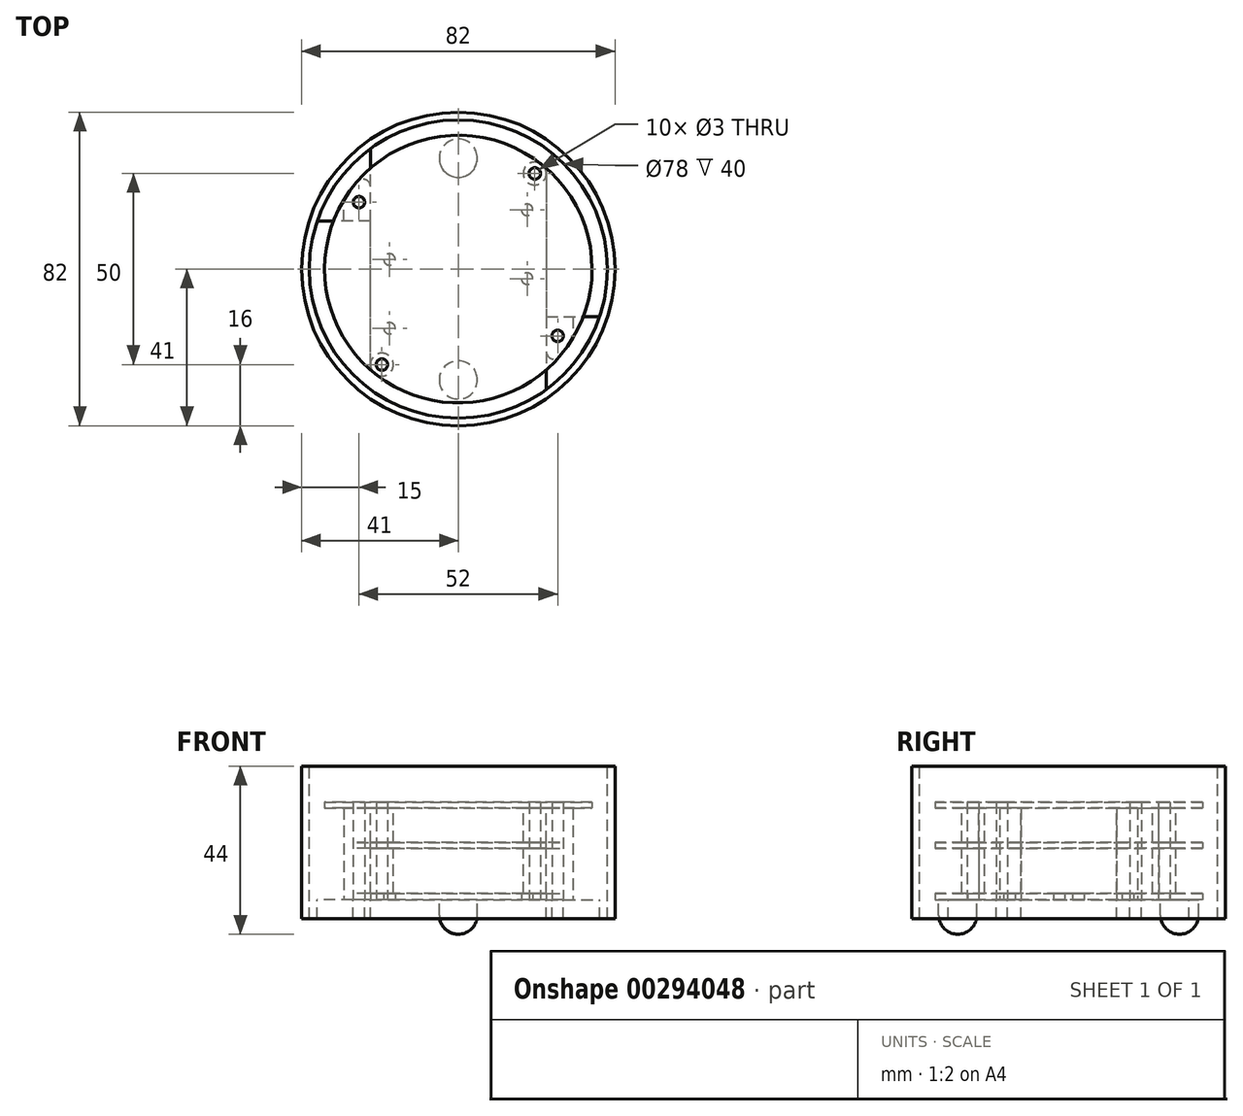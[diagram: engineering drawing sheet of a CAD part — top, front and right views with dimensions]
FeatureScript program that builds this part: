
annotation { "Feature Type Name" : "Feature", "Feature Type Description" : "" }
export const myFeature = defineFeature(function(context is Context, id is Id, definition is map)
    precondition{}
    {
        {
            var Q0;
            Q0=qCreatedBy(makeId("Top.planeOp"),FACE);
            var sketch = newSketch(context, id + "F0", { "sketchPlane" : qUnion([Q0])});
            skPoint(sketch, "E0.middle", {"position": v(0, 0) * mm});
            skLineSegment(sketch, "E1", {"start": v(0, 0) * mm, "end": v(0, 30) * mm, "construction": true});
            skLineSegment(sketch, "E2", {"start": v(0, 0) * mm, "end": v(-11.22, 0) * mm, "construction": true});
            skCircle(sketch, "E3", {"center": v(-18, 2.5) * mm, "radius": 1.5 * mm});
            skCircle(sketch, "E4", {"center": v(-18, -15.5) * mm, "radius": 1.5 * mm});
            skLineSegment(sketch, "E5", {"start": v(-18, -15.5) * mm, "end": v(-18, 2.5) * mm, "construction": true});
            skCircle(sketch, "E6.1.0", {"center": v(18, -2.5) * mm, "radius": 1.5 * mm});
            skCircle(sketch, "E6.1.1", {"center": v(18, 15.5) * mm, "radius": 1.5 * mm});
            skLineSegment(sketch, "E7", {"start": v(-23, -26.38) * mm, "end": v(-23, 12.5) * mm});
            skLineSegment(sketch, "E8", {"start": v(-23, 12.5) * mm, "end": v(-30, 12.5) * mm});
            skLineSegment(sketch, "E9", {"start": v(-30, 12.5) * mm, "end": v(-30, 18.03) * mm});
            skArc(sketch, "E10", {"start": v(-23, -26.38) * mm, "mid": v(5.45, -34.57) * mm, "end": v(30, -18.03) * mm});
            skLineSegment(sketch, "E11.1.0", {"start": v(23, 26.38) * mm, "end": v(23, -12.5) * mm});
            skLineSegment(sketch, "E11.1.1", {"start": v(23, -12.5) * mm, "end": v(30, -12.5) * mm});
            skLineSegment(sketch, "E11.1.2", {"start": v(30, -12.5) * mm, "end": v(30, -18.03) * mm});
            skArc(sketch, "E12.trimOffspring", {"start": v(23, 26.38) * mm, "mid": v(-5.45, 34.57) * mm, "end": v(-30, 18.03) * mm});
            skLineSegment(sketch, "E13", {"start": v(-18, -6.5) * mm, "end": v(-34.57, -6.5) * mm, "construction": true});
            skPoint(sketch, "E13.endSnap0", {"position": v(-18, -6.5) * mm});
            skCircle(sketch, "E14", {"center": v(26, -17.5) * mm, "radius": 1.5 * mm});
            skCircle(sketch, "E15.1.0", {"center": v(-26, 17.5) * mm, "radius": 1.5 * mm});
            skCircle(sketch, "E16", {"center": v(20, 25) * mm, "radius": 1.5 * mm});
            skCircle(sketch, "E17.1.0", {"center": v(-20, -25) * mm, "radius": 1.5 * mm});
            skSolve(sketch);
        }
        {
            var Q0;
            Q0=makeQuery(id+"F0.imprint","IMPRINT",FACE,{"disambiguationData":[TD([[makeQuery(id+"F0.imprint","IMPRINT",EDGE,{"derivedFrom":sQuery(id+"F0.wireOp",EDGE,"E3")}),-1.0]])]});
            extrude(context, id + "F1", {"entities" : qUnion([Q0]), "depth" : 1.67 * mm});
        }
        {
            var Q0;
            Q0=makeQuery(id+"F1.opExtrude","CAP_FACE",FACE,{"disambiguationData":[OSD([sQuery(id+"F0.wireOp",EDGE,"E3"),sQuery(id+"F0.wireOp",EDGE,"E4"),sQuery(id+"F0.wireOp",EDGE,"E6.1.0"),sQuery(id+"F0.wireOp",EDGE,"E6.1.1"),sQuery(id+"F0.wireOp",EDGE,"E7"),sQuery(id+"F0.wireOp",EDGE,"E8"),sQuery(id+"F0.wireOp",EDGE,"E9"),sQuery(id+"F0.wireOp",EDGE,"E10"),sQuery(id+"F0.wireOp",EDGE,"E11.1.0"),sQuery(id+"F0.wireOp",EDGE,"E11.1.1"),sQuery(id+"F0.wireOp",EDGE,"E11.1.2"),sQuery(id+"F0.wireOp",EDGE,"E12.trimOffspring")])],"isStart":true});
            var sketch = newSketch(context, id + "F2", { "sketchPlane" : qUnion([Q0])});
            skLineSegment(sketch, "E18", {"start": v(0, 0) * mm, "end": v(-11.39, 0) * mm, "construction": true});
            skCircle(sketch, "E19", {"center": v(0, 29) * mm, "radius": 5 * mm});
            skLineSegment(sketch, "E20", {"start": v(0, 29) * mm, "end": v(0, 0) * mm, "construction": true});
            skCircle(sketch, "E21.MirrorC", {"center": v(0, -29) * mm, "radius": 5 * mm});
            skSolve(sketch);
        }
        {
            var Q0;
            Q0 = qSketchRegion(id + "F2", true);
            extrude(context, id + "F3", {"entities" : qUnion([Q0]), "operationType" : NewBodyOperationType.ADD, "depth" : 9 * mm});
        }
        {
            var Q0;
            Q0=makeQuery(id+"F3.opExtrude","CAP_EDGE",EDGE,{"disambiguationData":[OSD([sQuery(id+"F2.wireOp",EDGE,"E19")])],"isStart":false});
            var Q1;
            Q1=makeQuery(id+"F3.opExtrude","CAP_EDGE",EDGE,{"disambiguationData":[OSD([sQuery(id+"F2.wireOp",EDGE,"E21.MirrorC")])],"isStart":false});
            fillet(context, id + "F4", {"entities" : qUnion([Q0, Q1]), "radius" : 5 * mm, "tangentPropagation" : true, "allowEdgeOverflow" : false});
        }
        {
            var Q0;
            Q0=qCreatedBy(makeId("Top.planeOp"),FACE);
            cPlane(context, id + "F5", {"entities" : qUnion([Q0]), "cplaneType" : CPlaneType.OFFSET, "offset" : 15 * mm, "width" : 150 * mm, "height" : 150 * mm});
        }
        {
            var Q0;
            Q0=qCreatedBy(id+"F5.planeOp",FACE);
            var sketch = newSketch(context, id + "F6", { "sketchPlane" : qUnion([Q0])});
            skLineSegment(sketch, "E22.0", {"start": v(-23, -26.38) * mm, "end": v(-23, 12.5) * mm});
            skLineSegment(sketch, "E23.0", {"start": v(-23, 12.5) * mm, "end": v(-30, 12.5) * mm});
            skArc(sketch, "E24.0", {"start": v(23, 26.38) * mm, "mid": v(-5.45, 34.57) * mm, "end": v(-30, 18.03) * mm});
            skLineSegment(sketch, "E25.0", {"start": v(-30, 12.5) * mm, "end": v(-30, 18.03) * mm});
            skLineSegment(sketch, "E26.0", {"start": v(23, 26.38) * mm, "end": v(23, -12.5) * mm});
            skCircle(sketch, "E27.0", {"center": v(-26, 17.5) * mm, "radius": 1.5 * mm});
            skCircle(sketch, "E28.0", {"center": v(20, 25) * mm, "radius": 1.5 * mm});
            skCircle(sketch, "E29.0", {"center": v(26, -17.5) * mm, "radius": 1.5 * mm});
            skCircle(sketch, "E30.0", {"center": v(-20, -25) * mm, "radius": 1.5 * mm});
            skArc(sketch, "E31.0", {"start": v(-23, -26.38) * mm, "mid": v(5.45, -34.57) * mm, "end": v(30, -18.03) * mm});
            skLineSegment(sketch, "E32.0", {"start": v(23, -12.5) * mm, "end": v(30, -12.5) * mm});
            skLineSegment(sketch, "E33.0", {"start": v(30, -12.5) * mm, "end": v(30, -18.03) * mm});
            skSolve(sketch);
        }
        {
            var Q0;
            Q0 = qSketchRegion(id + "F6", true);
            extrude(context, id + "F7", {"entities" : qUnion([Q0]), "oppositeDirection" : true, "depth" : 1.5 * mm});
        }
        {
            var Q0;
            Q0=makeQuery(id+"F7.opExtrude","CAP_FACE",FACE,{"disambiguationData":[OSD([sQuery(id+"F6.wireOp",EDGE,"E22.0"),sQuery(id+"F6.wireOp",EDGE,"E23.0"),sQuery(id+"F6.wireOp",EDGE,"E24.0"),sQuery(id+"F6.wireOp",EDGE,"E25.0"),sQuery(id+"F6.wireOp",EDGE,"E26.0"),sQuery(id+"F6.wireOp",EDGE,"E27.0"),sQuery(id+"F6.wireOp",EDGE,"E28.0"),sQuery(id+"F6.wireOp",EDGE,"E29.0"),sQuery(id+"F6.wireOp",EDGE,"E30.0"),sQuery(id+"F6.wireOp",EDGE,"E31.0"),sQuery(id+"F6.wireOp",EDGE,"E32.0"),sQuery(id+"F6.wireOp",EDGE,"E33.0")])],"isStart":false});
            var sketch = newSketch(context, id + "F8", { "sketchPlane" : qUnion([Q0])});
            skCircle(sketch, "E34.0", {"center": v(-26, -17.5) * mm, "radius": 1.5 * mm});
            skLineSegment(sketch, "E35.0", {"start": v(-23, -12.5) * mm, "end": v(-30, -12.5) * mm});
            skLineSegment(sketch, "E36.0", {"start": v(-30, -12.5) * mm, "end": v(-30, -18.03) * mm});
            skArc(sketch, "E37.0", {"start": v(-23, -26.38) * mm, "mid": v(-26.83, -22.48) * mm, "end": v(-30, -18.03) * mm});
            skCircle(sketch, "E38.0", {"center": v(20, -25) * mm, "radius": 1.5 * mm});
            skCircle(sketch, "E39", {"center": v(20, -25) * mm, "radius": 3 * mm});
            skCircle(sketch, "E40.0", {"center": v(-20, 25) * mm, "radius": 1.5 * mm});
            skCircle(sketch, "E41.0", {"center": v(26, 17.5) * mm, "radius": 1.5 * mm});
            skCircle(sketch, "E42", {"center": v(-20, 25) * mm, "radius": 3 * mm});
            skPoint(sketch, "E43.orphan", {"position": v(23, -26.38) * mm});
            skLineSegment(sketch, "E44.0", {"start": v(30, 12.5) * mm, "end": v(30, 18.03) * mm});
            skLineSegment(sketch, "E45.0", {"start": v(23, 12.5) * mm, "end": v(30, 12.5) * mm});
            skArc(sketch, "E46.0", {"start": v(23, 26.38) * mm, "mid": v(26.83, 22.48) * mm, "end": v(30, 18.03) * mm});
            skPoint(sketch, "E47.orphan", {"position": v(-23, 26.38) * mm});
            skLineSegment(sketch, "E48", {"start": v(-23, -12.5) * mm, "end": v(-23, -26.38) * mm});
            skLineSegment(sketch, "E49", {"start": v(23, 12.5) * mm, "end": v(23, 26.38) * mm});
            skSolve(sketch);
        }
        {
            var Q0;
            Q0 = qSketchRegion(id + "F8", true);
            extrude(context, id + "F9", {"entities" : qUnion([Q0]), "operationType" : NewBodyOperationType.ADD, "depth" : (13.5 - 1.67) * mm});
        }
        {
            var Q0;
            Q0=makeQuery(id+"F9.opExtrude","SWEPT_EDGE",EDGE,{"disambiguationData":[OSD([sQuery(id+"F6.wireOp",EDGE,"E31.0"),sQuery(id+"F8.wireOp",EDGE,"E46.0"),sQuery(id+"F8.wireOp",EDGE,"E49")])]});
            var Q1;
            Q1=makeQuery(id+"F9.opExtrude","SWEPT_EDGE",EDGE,{"disambiguationData":[OSD([sQuery(id+"F6.wireOp",EDGE,"E24.0"),sQuery(id+"F8.wireOp",EDGE,"E37.0"),sQuery(id+"F8.wireOp",EDGE,"E48")])]});
            fillet(context, id + "F10", {"entities" : qUnion([Q0, Q1]), "radius" : 2 * mm, "tangentPropagation" : true, "allowEdgeOverflow" : false});
        }
        {
            var Q0;
            Q0=makeQuery(id+"F7.opExtrude","SWEPT_EDGE",EDGE,{"disambiguationData":[OSD([sQuery(id+"F6.wireOp",EDGE,"E22.0"),sQuery(id+"F6.wireOp",EDGE,"E31.0")])]});
            var Q1;
            Q1=makeQuery(id+"F7.opExtrude","SWEPT_EDGE",EDGE,{"disambiguationData":[OSD([sQuery(id+"F6.wireOp",EDGE,"E24.0"),sQuery(id+"F6.wireOp",EDGE,"E26.0")])]});
            fillet(context, id + "F11", {"entities" : qUnion([Q0, Q1]), "radius" : 3 * mm, "tangentPropagation" : true, "allowEdgeOverflow" : false});
        }
        {
            var Q0;
            Q0=makeQuery(id+"F7.opExtrude","CAP_FACE",FACE,{"disambiguationData":[OSD([sQuery(id+"F6.wireOp",EDGE,"E22.0"),sQuery(id+"F6.wireOp",EDGE,"E23.0"),sQuery(id+"F6.wireOp",EDGE,"E24.0"),sQuery(id+"F6.wireOp",EDGE,"E25.0"),sQuery(id+"F6.wireOp",EDGE,"E26.0"),sQuery(id+"F6.wireOp",EDGE,"E27.0"),sQuery(id+"F6.wireOp",EDGE,"E28.0"),sQuery(id+"F6.wireOp",EDGE,"E29.0"),sQuery(id+"F6.wireOp",EDGE,"E30.0"),sQuery(id+"F6.wireOp",EDGE,"E31.0"),sQuery(id+"F6.wireOp",EDGE,"E32.0"),sQuery(id+"F6.wireOp",EDGE,"E33.0")])],"isStart":true});
            cPlane(context, id + "F12", {"entities" : qUnion([Q0]), "cplaneType" : CPlaneType.OFFSET, "offset" : 9 * mm, "width" : 150 * mm, "height" : 150 * mm});
        }
        {
            var Q0;
            Q0=qCreatedBy(id+"F12.planeOp",FACE);
            var sketch = newSketch(context, id + "F13", { "sketchPlane" : qUnion([Q0])});
            skArc(sketch, "E50.0", {"start": v(21.88, 27.32) * mm, "mid": v(-6.17, 34.45) * mm, "end": v(-30, 18.03) * mm});
            skArc(sketch, "E51.0", {"start": v(-30, 18.03) * mm, "mid": v(6.17, -34.45) * mm, "end": v(21.88, 27.32) * mm});
            skCircle(sketch, "E52.0", {"center": v(-26, 17.5) * mm, "radius": 1.5 * mm});
            skCircle(sketch, "E53.0", {"center": v(26, -17.5) * mm, "radius": 1.5 * mm});
            skCircle(sketch, "E54.0", {"center": v(-20, -25) * mm, "radius": 1.5 * mm});
            skCircle(sketch, "E55.0", {"center": v(20, 25) * mm, "radius": 1.5 * mm});
            skSolve(sketch);
        }
        {
            var Q0;
            Q0 = qSketchRegion(id + "F13", true);
            extrude(context, id + "F14", {"entities" : qUnion([Q0]), "depth" : 1.5 * mm});
        }
        {
            var Q0;
            Q0=makeQuery(id+"F14.opExtrude","CAP_FACE",FACE,{"disambiguationData":[OSD([sQuery(id+"F13.wireOp",EDGE,"E50.0"),sQuery(id+"F13.wireOp",EDGE,"f83100b9-3e47-460e-aa8e-1eb1b48f4dbf.0"),sQuery(id+"F13.wireOp",EDGE,"13f75684-cac0-4866-9a5c-2c3870ba1323.0"),sQuery(id+"F13.wireOp",EDGE,"d16af709-d34b-4538-ba98-1b08311f0eb7.0"),sQuery(id+"F13.wireOp",EDGE,"ec843569-b585-4750-a928-a7ac049e8fc0.0"),sQuery(id+"F13.wireOp",EDGE,"E51.0"),sQuery(id+"F13.wireOp",EDGE,"d7239e21-ecb2-416b-87c1-86b7ac30b069.0"),sQuery(id+"F13.wireOp",EDGE,"84af4c3a-e860-473a-a5bc-9a3056a9ac3e.0"),sQuery(id+"F13.wireOp",EDGE,"2ce0cd4b-7b7c-49db-a94b-4abc7f83e37b.0"),sQuery(id+"F13.wireOp",EDGE,"dbe12760-2b80-4098-a8ef-f66ca4a46cf9.0"),sQuery(id+"F13.wireOp",EDGE,"E52.0"),sQuery(id+"F13.wireOp",EDGE,"E53.0")])],"isStart":true});
            var sketch = newSketch(context, id + "F15", { "sketchPlane" : qUnion([Q0])});
            skLineSegment(sketch, "E56.0", {"start": v(23, 12.5) * mm, "end": v(30, 12.5) * mm});
            skLineSegment(sketch, "E57.0", {"start": v(30, 12.5) * mm, "end": v(30, 18.03) * mm});
            skArc(sketch, "E58.0", {"start": v(26.52, 22.85) * mm, "mid": v(28.36, 20.51) * mm, "end": v(30, 18.03) * mm});
            skArc(sketch, "E59.0", {"start": v(26.52, 22.85) * mm, "mid": v(24.3, 23.42) * mm, "end": v(23, 21.54) * mm});
            skLineSegment(sketch, "E60.0", {"start": v(23, 12.5) * mm, "end": v(23, 21.54) * mm});
            skLineSegment(sketch, "E61.0", {"start": v(-23, -12.5) * mm, "end": v(-23, -21.54) * mm});
            skArc(sketch, "E62.0", {"start": v(-26.52, -22.85) * mm, "mid": v(-24.3, -23.42) * mm, "end": v(-23, -21.54) * mm});
            skArc(sketch, "E63.0", {"start": v(-26.52, -22.85) * mm, "mid": v(-28.36, -20.51) * mm, "end": v(-30, -18.03) * mm});
            skLineSegment(sketch, "E64.0", {"start": v(-30, -12.5) * mm, "end": v(-30, -18.03) * mm});
            skLineSegment(sketch, "E65.0", {"start": v(-23, -12.5) * mm, "end": v(-30, -12.5) * mm});
            skCircle(sketch, "E66.0", {"center": v(20, -25) * mm, "radius": 3 * mm});
            skCircle(sketch, "E67.0", {"center": v(-20, 25) * mm, "radius": 3 * mm});
            skCircle(sketch, "E68.0", {"center": v(-20, 25) * mm, "radius": 1.5 * mm});
            skCircle(sketch, "E69.0", {"center": v(20, -25) * mm, "radius": 1.5 * mm});
            skCircle(sketch, "E70.0", {"center": v(26, 17.5) * mm, "radius": 1.5 * mm});
            skCircle(sketch, "E71.0", {"center": v(-26, -17.5) * mm, "radius": 1.5 * mm});
            skSolve(sketch);
        }
        {
            var Q0;
            Q0 = qSketchRegion(id + "F15", true);
            extrude(context, id + "F16", {"entities" : qUnion([Q0]), "operationType" : NewBodyOperationType.ADD, "depth" : 9 * mm});
        }
        {
            var Q0;
            Q0=makeQuery(id+"F1.opExtrude","CAP_FACE",FACE,{"disambiguationData":[OSD([sQuery(id+"F0.wireOp",EDGE,"E3"),sQuery(id+"F0.wireOp",EDGE,"E4"),sQuery(id+"F0.wireOp",EDGE,"E6.1.0"),sQuery(id+"F0.wireOp",EDGE,"E6.1.1"),sQuery(id+"F0.wireOp",EDGE,"E7"),sQuery(id+"F0.wireOp",EDGE,"E8"),sQuery(id+"F0.wireOp",EDGE,"E9"),sQuery(id+"F0.wireOp",EDGE,"E10"),sQuery(id+"F0.wireOp",EDGE,"E11.1.0"),sQuery(id+"F0.wireOp",EDGE,"E11.1.1"),sQuery(id+"F0.wireOp",EDGE,"E11.1.2"),sQuery(id+"F0.wireOp",EDGE,"E12.trimOffspring"),sQuery(id+"F0.wireOp",EDGE,"E14"),sQuery(id+"F0.wireOp",EDGE,"E15.1.0"),sQuery(id+"F0.wireOp",EDGE,"E16"),sQuery(id+"F0.wireOp",EDGE,"E17.1.0")])],"isStart":true});
            var sketch = newSketch(context, id + "F17", { "sketchPlane" : qUnion([Q0])});
            skCircle(sketch, "E72", {"center": v(0, 0) * mm, "radius": 41 * mm});
            skArc(sketch, "E73", {"start": v(23, 31.5) * mm, "mid": v(-23.08, 31.44) * mm, "end": v(-36.94, -12.5) * mm});
            skLineSegment(sketch, "E74", {"start": v(41, 0) * mm, "end": v(39, 0) * mm, "construction": true});
            skLineSegment(sketch, "E75.0", {"start": v(23, 12.5) * mm, "end": v(30, 12.5) * mm});
            skLineSegment(sketch, "E76", {"start": v(23, 12.5) * mm, "end": v(23, 31.5) * mm});
            skLineSegment(sketch, "E77", {"start": v(30, 12.5) * mm, "end": v(36.94, 12.5) * mm});
            skLineSegment(sketch, "E78", {"start": v(-23, -12.5) * mm, "end": v(-23, -31.5) * mm});
            skLineSegment(sketch, "E79", {"start": v(-23, -12.5) * mm, "end": v(-36.94, -12.5) * mm});
            skArc(sketch, "E80.trimOffspring", {"start": v(-23, -31.5) * mm, "mid": v(23.08, -31.44) * mm, "end": v(36.94, 12.5) * mm});
            skCircle(sketch, "E81.0", {"center": v(-26, -17.5) * mm, "radius": 1.5 * mm});
            skCircle(sketch, "E82.0", {"center": v(26, 17.5) * mm, "radius": 1.5 * mm});
            skSolve(sketch);
        }
        {
            var Q0;
            Q0=makeQuery(id+"F17.imprint","IMPRINT",FACE,{"disambiguationData":[TD([[makeQuery(id+"F17.imprint","IMPRINT",EDGE,{"derivedFrom":sQuery(id+"F17.wireOp",EDGE,"E72")}),1.0]])]});
            var Q1;
            {var subQ2=sQuery(id+"F17.wireOp",EDGE,"E75.0");Q1=makeQuery(id+"F17.imprint","IMPRINT",FACE,{"disambiguationData":[TD([[makeQuery(id+"F17.imprint","IMPRINT",EDGE,{"derivedFrom":subQ2}),1.0]])]});}
            var Q2;
            Q2=makeQuery(id+"F17.imprint","IMPRINT",FACE,{"disambiguationData":[TD([[makeQuery(id+"F17.imprint","IMPRINT",EDGE,{"derivedFrom":sQuery(id+"F17.wireOp",EDGE,"E81.0")}),1.0]])]});
            extrude(context, id + "F18", {"entities" : qUnion([Q0, Q1, Q2]), "depth" : 5 * mm});
        }
        {
            var Q0;
            Q0=makeQuery(id+"F18.opExtrude","CAP_FACE",FACE,{"disambiguationData":[OSD([sQuery(id+"F17.wireOp",EDGE,"E72"),sQuery(id+"F17.wireOp",EDGE,"fa01af37-9df1-4d82-b2de-7d3f027df5ed.0"),sQuery(id+"F17.wireOp",EDGE,"5ca2957c-19f2-429e-8de8-c1ab68f11df0.0"),sQuery(id+"F17.wireOp",EDGE,"c80b1a02-b8bc-4ad3-b2f8-2978f5755b6d.0"),sQuery(id+"F17.wireOp",EDGE,"93c5222f-73d5-4699-a0a4-99e908de7359.0")])],"isStart":true});
            var sketch = newSketch(context, id + "F19", { "sketchPlane" : qUnion([Q0])});
            skCircle(sketch, "E83.0", {"center": v(0, 0) * mm, "radius": 41 * mm});
            skCircle(sketch, "E84", {"center": v(0, 0) * mm, "radius": 39 * mm});
            skLineSegment(sketch, "E85", {"start": v(39, 0) * mm, "end": v(41, 0) * mm, "construction": true});
            skSolve(sketch);
        }
        {
            var Q0;
            Q0 = qSketchRegion(id + "F19", true);
            extrude(context, id + "F20", {"entities" : qUnion([Q0]), "operationType" : NewBodyOperationType.ADD, "depth" : 35 * mm});
        }
    });
